# Revit family: Haworth_Epure_MeetingTable_EU_PRELIMINARY
name_source: partatom
category: Furniture
units: mm (PartAtom-declared; Revit-internal decimal feet)

## family parameters
Always vertical = Yes
Cut with Voids When Loaded = No
OmniClass Number = 23.40.70.14.64.11
OmniClass Title = Office Furniture
Room Calculation Point = No
Shared = No
Work Plane-Based = No

## types (7) — shared parameters
Actual Height = 73 cm
Assembly Code = E2020200
Description = Haworth - Epure - Meeting Table
Flip Top Finish = Haworth _ Paint _ Metallic Silver
Leg Height = 70 cm
Manufacturer = Haworth
Model = EUMTXXXX
Revision Number = 1
Size = Verify Final Dim.w/ Haworth
Trim Finish = Haworth _ Metal _ Structured White EC
URL = https://www.haworth.com
URL - Product = https://www.haworth.com
Warranty = http://www.haworth.com

## per-type parameters (varying)
| type | Actual Depth | Actual Width | Flip Top Cable Outlet | Large | Large Corner Rounded | Large Corner Square | Large Drop Table | Medium Drop Table | Not Flip Top | Small | Small Corner Rounded | Small Corner Square | Small Drop Table |
| 109 x 109 | 109 cm | 109 cm | No | No | No | No | No | No | Yes | Yes | No | No | Yes |
| 149 x 149 | 149 cm | 149 cm | No | No | No | No | Yes | No | Yes | Yes | No | No | No |
| 120 x 120 | 120 cm | 120 cm | No | No | No | No | No | Yes | Yes | Yes | No | No | No |
| 200 x 100 - Rounded | 100 cm | 200 cm | Yes | Yes | No | No | No | No | No | No | Yes | No | No |
| 200 x 100 - Squared | 100 cm | 200 cm | No | Yes | No | No | No | No | Yes | No | No | Yes | No |
| 240 x 120 - Rounded | 120 cm | 240 cm | No | Yes | Yes | No | No | No | Yes | No | No | No | No |
| 240 x 120 - Squared | 120 cm | 240 cm | Yes | Yes | No | Yes | No | No | No | No | No | No | No |

## geometry (parser evidence)
native form markers: Sweep x13
no freeform markers — native parametric forms only
